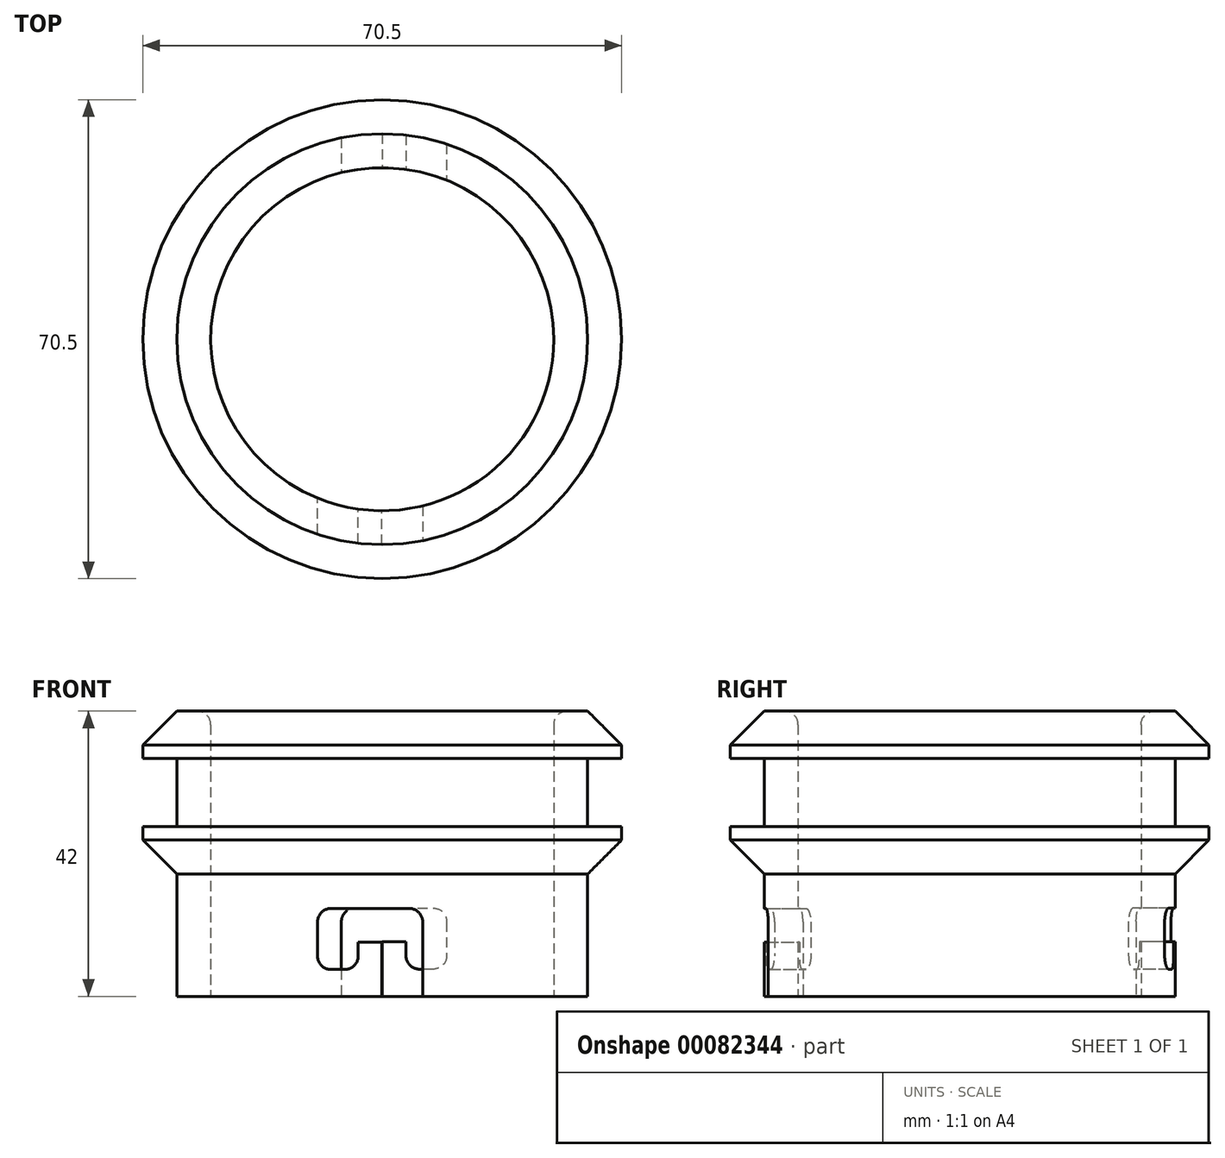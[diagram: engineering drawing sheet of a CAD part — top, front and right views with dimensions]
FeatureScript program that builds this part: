
annotation { "Feature Type Name" : "Feature", "Feature Type Description" : "" }
export const myFeature = defineFeature(function(context is Context, id is Id, definition is map)
    precondition{}
    {
        {
            var Q0;
            Q0=qCreatedBy(makeId("Top.planeOp"),FACE);
            var sketch = newSketch(context, id + "F0", { "sketchPlane" : qUnion([Q0])});
            skCircle(sketch, "E0", {"center": v(0, 0) * mm, "radius": 30.25 * mm});
            skCircle(sketch, "E1", {"center": v(0, 0) * mm, "radius": 25.25 * mm});
            skSolve(sketch);
        }
        {
            var Q0;
            Q0=makeQuery(id+"F0.imprint","IMPRINT",FACE,{"disambiguationData":[TD([[makeQuery(id+"F0.imprint","IMPRINT",EDGE,{"derivedFrom":sQuery(id+"F0.wireOp",EDGE,"E0")}),1.0]])]});
            extrude(context, id + "F1", {"entities" : qUnion([Q0]), "depth" : 18 * mm});
        }
        {
            var Q0;
            Q0=makeQuery(id+"F1.opExtrude","CAP_FACE",FACE,{"disambiguationData":[OSD([sQuery(id+"F0.wireOp",EDGE,"E0"),sQuery(id+"F0.wireOp",EDGE,"E1")])],"isStart":false});
            var sketch = newSketch(context, id + "F2", { "sketchPlane" : qUnion([Q0])});
            skCircle(sketch, "E2", {"center": v(0, 0) * mm, "radius": 35.25 * mm});
            skCircle(sketch, "E3", {"center": v(0, 0) * mm, "radius": 25.25 * mm});
            skSolve(sketch);
        }
        {
            var Q0;
            Q0=makeQuery(id+"F2.imprint","IMPRINT",FACE,{"disambiguationData":[TD([[makeQuery(id+"F2.imprint","IMPRINT",EDGE,{"derivedFrom":sQuery(id+"F2.wireOp",EDGE,"E2")}),1.0]])]});
            var Q1;
            Q1=makeQuery(id+"F2.imprint","IMPRINT",FACE,{"disambiguationData":[TD([[makeQuery(id+"F2.imprint","IMPRINT",EDGE,{"derivedFrom":sQuery(id+"F2.wireOp",EDGE,"E3")}),-1.0]])]});
            extrude(context, id + "F3", {"entities" : qUnion([Q0, Q1]), "operationType" : NewBodyOperationType.ADD, "depth" : 7 * mm});
        }
        {
            var Q0;
            Q0=makeQuery(id+"F3.opExtrude","CAP_FACE",FACE,{"disambiguationData":[OSD([sQuery(id+"F2.wireOp",EDGE,"E2"),sQuery(id+"F2.wireOp",EDGE,"E3")])],"isStart":false});
            var sketch = newSketch(context, id + "F4", { "sketchPlane" : qUnion([Q0])});
            skCircle(sketch, "E4", {"center": v(0, 0) * mm, "radius": 30.25 * mm});
            skCircle(sketch, "E5", {"center": v(0, 0) * mm, "radius": 25.25 * mm});
            skSolve(sketch);
        }
        {
            var Q0;
            Q0=makeQuery(id+"F4.imprint","IMPRINT",FACE,{"disambiguationData":[TD([[makeQuery(id+"F4.imprint","IMPRINT",EDGE,{"derivedFrom":sQuery(id+"F4.wireOp",EDGE,"E4")}),1.0]])]});
            extrude(context, id + "F5", {"entities" : qUnion([Q0]), "operationType" : NewBodyOperationType.ADD, "depth" : 10 * mm});
        }
        {
            var Q0;
            Q0=makeQuery(id+"F5.opExtrude","CAP_FACE",FACE,{"disambiguationData":[OSD([sQuery(id+"F4.wireOp",EDGE,"E4"),sQuery(id+"F4.wireOp",EDGE,"E5")])],"isStart":false});
            var sketch = newSketch(context, id + "F6", { "sketchPlane" : qUnion([Q0])});
            skCircle(sketch, "E6", {"center": v(0, 0) * mm, "radius": 35.25 * mm});
            skCircle(sketch, "E7", {"center": v(0, 0) * mm, "radius": 25.25 * mm});
            skSolve(sketch);
        }
        {
            var Q0;
            Q0=makeQuery(id+"F6.imprint","IMPRINT",FACE,{"disambiguationData":[TD([[makeQuery(id+"F6.imprint","IMPRINT",EDGE,{"derivedFrom":sQuery(id+"F6.wireOp",EDGE,"E6")}),1.0]])]});
            var Q1;
            Q1=makeQuery(id+"F6.imprint","IMPRINT",FACE,{"disambiguationData":[TD([[makeQuery(id+"F6.imprint","IMPRINT",EDGE,{"derivedFrom":sQuery(id+"F6.wireOp",EDGE,"E7")}),-1.0]])]});
            extrude(context, id + "F7", {"entities" : qUnion([Q0, Q1]), "operationType" : NewBodyOperationType.ADD, "depth" : 7 * mm});
        }
        {
            var Q0;
            Q0=makeQuery(id+"F7.opExtrude","CAP_EDGE",EDGE,{"disambiguationData":[OSD([sQuery(id+"F6.wireOp",EDGE,"E7")])],"isStart":false});
            fillet(context, id + "F8", {"entities" : qUnion([Q0]), "radius" : 2 * mm, "tangentPropagation" : true, "allowEdgeOverflow" : false});
        }
        {
            var Q0;
            Q0=qCreatedBy(makeId("Front.planeOp"),FACE);
            var sketch = newSketch(context, id + "F9", { "sketchPlane" : qUnion([Q0])});
            skLineSegment(sketch, "E8", {"start": v(0, 0) * mm, "end": v(-6, 0) * mm});
            skLineSegment(sketch, "E9", {"start": v(-6, 0) * mm, "end": v(-6, 13) * mm});
            skLineSegment(sketch, "E10", {"start": v(-6, 13) * mm, "end": v(9.5, 13) * mm});
            skLineSegment(sketch, "E11", {"start": v(9.5, 13) * mm, "end": v(9.5, 4) * mm});
            skLineSegment(sketch, "E12", {"start": v(9.5, 4) * mm, "end": v(3.5, 4) * mm});
            skLineSegment(sketch, "E13", {"start": v(3.5, 4) * mm, "end": v(3.5, 8.01) * mm});
            skLineSegment(sketch, "E14", {"start": v(3.5, 8.01) * mm, "end": v(0, 8.01) * mm});
            skLineSegment(sketch, "E15", {"start": v(0, 8.01) * mm, "end": v(0, 0) * mm});
            skSolve(sketch);
        }
        {
            var Q0;
            Q0 = qSketchRegion(id + "F9", true);
            extrude(context, id + "F10", {"entities" : qUnion([Q0]), "operationType" : NewBodyOperationType.REMOVE, "oppositeDirection" : true, "depth" : 50 * mm});
        }
        {
            var Q0;
            Q0=makeQuery(id+"F10.boolean.opBoolean","COPY",EDGE,{"derivedFrom":makeQuery(id+"F10.opExtrude","SWEPT_EDGE",EDGE,{"disambiguationData":[OSD([sQuery(id+"F9.wireOp",EDGE,"E10"),sQuery(id+"F9.wireOp",EDGE,"E11")])]})});
            var Q1;
            Q1=makeQuery(id+"F10.boolean.opBoolean","COPY",EDGE,{"derivedFrom":makeQuery(id+"F10.opExtrude","SWEPT_EDGE",EDGE,{"disambiguationData":[OSD([sQuery(id+"F9.wireOp",EDGE,"E9"),sQuery(id+"F9.wireOp",EDGE,"E10")])]})});
            var Q2;
            Q2=makeQuery(id+"F10.boolean.opBoolean","COPY",EDGE,{"derivedFrom":makeQuery(id+"F10.opExtrude","SWEPT_EDGE",EDGE,{"disambiguationData":[OSD([sQuery(id+"F9.wireOp",EDGE,"E12"),sQuery(id+"F9.wireOp",EDGE,"E13")])]})});
            var Q3;
            Q3=makeQuery(id+"F10.boolean.opBoolean","COPY",EDGE,{"derivedFrom":makeQuery(id+"F10.opExtrude","SWEPT_EDGE",EDGE,{"disambiguationData":[OSD([sQuery(id+"F9.wireOp",EDGE,"E11"),sQuery(id+"F9.wireOp",EDGE,"E12")])]})});
            fillet(context, id + "F11", {"entities" : qUnion([Q0, Q1, Q2, Q3]), "radius" : 2 * mm, "tangentPropagation" : true, "allowEdgeOverflow" : false});
        }
        {
            var Q0;
            Q0=qCreatedBy(makeId("Front.planeOp"),FACE);
            var sketch = newSketch(context, id + "F12", { "sketchPlane" : qUnion([Q0])});
            skLineSegment(sketch, "E16", {"start": v(5.97, -0.05) * mm, "end": v(5.97, 12.95) * mm});
            skLineSegment(sketch, "E17.MirrorCS", {"start": v(5.97, 12.95) * mm, "end": v(-9.53, 12.95) * mm});
            skLineSegment(sketch, "E18.MirrorCS", {"start": v(-9.53, 12.95) * mm, "end": v(-9.53, 3.95) * mm});
            skLineSegment(sketch, "E19.MirrorCS", {"start": v(-9.53, 3.95) * mm, "end": v(-3.53, 3.95) * mm});
            skLineSegment(sketch, "E20.MirrorCS", {"start": v(-3.53, 3.95) * mm, "end": v(-3.53, 7.96) * mm});
            skLineSegment(sketch, "E21.MirrorCS", {"start": v(-3.53, 7.96) * mm, "end": v(-0.03, 7.96) * mm});
            skLineSegment(sketch, "E22.MirrorCS", {"start": v(-0.03, 7.96) * mm, "end": v(-0.03, -0.05) * mm});
            skLineSegment(sketch, "E23.MirrorCS", {"start": v(-0.03, -0.05) * mm, "end": v(5.97, -0.05) * mm});
            skSolve(sketch);
        }
        {
            var Q0;
            Q0 = qSketchRegion(id + "F12", true);
            extrude(context, id + "F13", {"entities" : qUnion([Q0]), "operationType" : NewBodyOperationType.REMOVE, "depth" : 50 * mm});
        }
        {
            var Q0;
            Q0=makeQuery(id+"F13.boolean.opBoolean","COPY",EDGE,{"derivedFrom":makeQuery(id+"F13.opExtrude","SWEPT_EDGE",EDGE,{"disambiguationData":[OSD([sQuery(id+"F12.wireOp",EDGE,"E17.MirrorCS"),sQuery(id+"F12.wireOp",EDGE,"E18.MirrorCS")])]})});
            var Q1;
            Q1=makeQuery(id+"F13.boolean.opBoolean","COPY",EDGE,{"derivedFrom":makeQuery(id+"F13.opExtrude","SWEPT_EDGE",EDGE,{"disambiguationData":[OSD([sQuery(id+"F12.wireOp",EDGE,"E18.MirrorCS"),sQuery(id+"F12.wireOp",EDGE,"E19.MirrorCS")])]})});
            var Q2;
            Q2=makeQuery(id+"F13.boolean.opBoolean","COPY",EDGE,{"derivedFrom":makeQuery(id+"F13.opExtrude","SWEPT_EDGE",EDGE,{"disambiguationData":[OSD([sQuery(id+"F12.wireOp",EDGE,"E19.MirrorCS"),sQuery(id+"F12.wireOp",EDGE,"E20.MirrorCS")])]})});
            var Q3;
            Q3=makeQuery(id+"F13.boolean.opBoolean","COPY",EDGE,{"derivedFrom":makeQuery(id+"F13.opExtrude","SWEPT_EDGE",EDGE,{"disambiguationData":[OSD([sQuery(id+"F12.wireOp",EDGE,"E16"),sQuery(id+"F12.wireOp",EDGE,"E17.MirrorCS")])]})});
            fillet(context, id + "F14", {"entities" : qUnion([Q0, Q1, Q2, Q3]), "radius" : 2 * mm, "tangentPropagation" : true, "allowEdgeOverflow" : false});
        }
        {
            var Q0;
            Q0=makeQuery(id+"F3.opExtrude","CAP_EDGE",EDGE,{"disambiguationData":[OSD([sQuery(id+"F2.wireOp",EDGE,"E2")])],"isStart":true});
            var Q1;
            Q1=makeQuery(id+"F7.opExtrude","CAP_EDGE",EDGE,{"disambiguationData":[OSD([sQuery(id+"F6.wireOp",EDGE,"E6")])],"isStart":false});
            chamfer(context, id + "F15", {"entities" : qUnion([Q0, Q1]), "chamferType" : ChamferType.TWO_OFFSETS, "width1" : 5 * mm, "oppositeDirection" : false, "width2" : 5 * mm, "tangentPropagation" : true});
        }
    });
